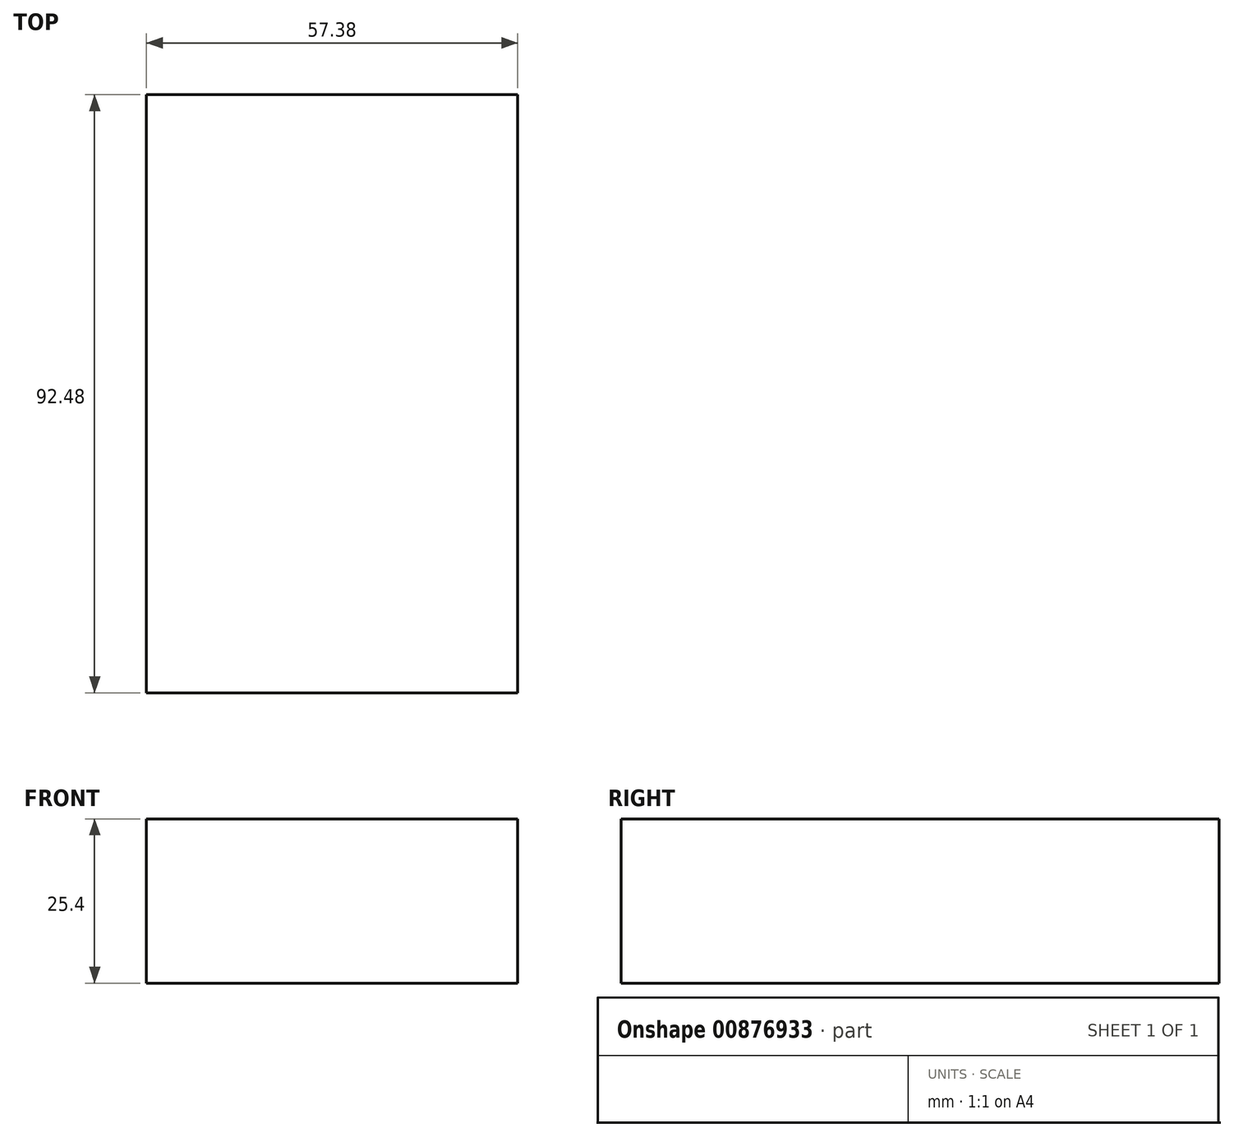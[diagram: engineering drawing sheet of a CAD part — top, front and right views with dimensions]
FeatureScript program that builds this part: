
annotation { "Feature Type Name" : "Feature", "Feature Type Description" : "" }
export const myFeature = defineFeature(function(context is Context, id is Id, definition is map)
    precondition{}
    {
        {
            var Q0;
            Q0=qCreatedBy(makeId("Top.planeOp"),FACE);
            var sketch = newSketch(context, id + "F0", { "sketchPlane" : qUnion([Q0])});
            skLineSegment(sketch, "E0.bottom", {"start": v(28.7, 46.24) * mm, "end": v(-28.7, 46.24) * mm});
            skLineSegment(sketch, "E0.top", {"start": v(28.7, -46.24) * mm, "end": v(-28.7, -46.24) * mm});
            skLineSegment(sketch, "E0.left", {"start": v(28.7, 46.24) * mm, "end": v(28.7, -46.24) * mm});
            skLineSegment(sketch, "E0.right", {"start": v(-28.7, 46.24) * mm, "end": v(-28.7, -46.24) * mm});
            skPoint(sketch, "E0.middle", {"position": v(0, 0) * mm});
            skSolve(sketch);
        }
        {
            var Q0;
            Q0=makeQuery(id+"F0.imprint","IMPRINT",FACE,{"disambiguationData":[TD([[makeQuery(id+"F0.imprint","IMPRINT",EDGE,{"derivedFrom":sQuery(id+"F0.wireOp",EDGE,"E0.bottom")}),1.0]])]});
            extrude(context, id + "F1", {"entities" : qUnion([Q0]), "depth" : 25.4 * mm, "offsetDistance" : 25.4 * mm});
        }
    });
